annotation { "Feature Type Name" : "Feature", "Feature Type Description" : "" }
export const myFeature = defineFeature(function(context is Context, id is Id, definition is map)
    precondition{}
    {
        {
            var Q0;
            Q0=qCreatedBy(makeId("Front.planeOp"),FACE);
            var sketch = newSketch(context, id + "F0", { "sketchPlane" : qUnion([Q0])});
            skFitSpline(sketch, "E0", {"points": [v(-3.73, -24.98) * mm, v(-7.65, -24.83) * mm, v(-12.44, -18.15) * mm, v(-12.87, -5.52) * mm, v(-17.38, -7.12) * mm, v(-18.97, -20.91) * mm, v(-14.76, -31.66) * mm, v(-14.04, -37.46) * mm, v(-21.44, -52.13) * mm, v(-22.46, -57.8) * mm, v(-21.59, -62.3) * mm, v(-19.4, -65.05) * mm, v(-17.23, -67.38) * mm, v(-11.57, -70.43) * mm, v(-1.26, -72.9) * mm, v(9.49, -73.19) * mm, v(18.93, -67.96) * mm, v(21.69, -60.84) * mm, v(15.73, -44.43) * mm, v(14.72, -38.92) * mm, v(18.2, -30.5) * mm, v(17.33, -25.7) * mm, v(12.97, -30.93) * mm, v(5.57, -30.5) * mm, v(4.26, -24.54) * mm], "startDerivative": vector(-129.19, -19.7) * mm, "endDerivative": vector(5.95, 184.87) * mm});
            skLineSegment(sketch, "E1", {"start": v(-3.73, -24.98) * mm, "end": v(4.26, -25.17) * mm});
            skLineSegment(sketch, "E2", {"start": v(4.26, -25.17) * mm, "end": v(4.26, -24.54) * mm});
            skSolve(sketch);
        }
        {
            var Q0;
            Q0 = qSketchRegion(id + "F0", true);
            extrude(context, id + "F1", {"entities" : qUnion([Q0]), "depth" : 7.62 * mm});
        }
        {
            var Q0;
            Q0=makeQuery(id+"F1.opExtrude","CAP_FACE",FACE,{"disambiguationData":[OSD([sQuery(id+"F0.wireOp",EDGE,"E0"),sQuery(id+"F0.wireOp",EDGE,"E1")])],"isStart":false});
            var sketch = newSketch(context, id + "F2", { "sketchPlane" : qUnion([Q0])});
            skLineSegment(sketch, "E3.bottom", {"start": v(-10.16, -39.56) * mm, "end": v(10.16, -39.56) * mm});
            skLineSegment(sketch, "E3.top", {"start": v(-10.16, -44.4) * mm, "end": v(10.16, -44.4) * mm});
            skLineSegment(sketch, "E3.left", {"start": v(-10.16, -39.56) * mm, "end": v(-10.16, -44.4) * mm});
            skLineSegment(sketch, "E3.right", {"start": v(10.16, -39.56) * mm, "end": v(10.16, -44.4) * mm});
            skPoint(sketch, "E3.middle", {"position": v(0, -41.99) * mm});
            skSolve(sketch);
        }
        {
            var Q0;
            Q0 = qSketchRegion(id + "F2", true);
            extrude(context, id + "F3", {"entities" : qUnion([Q0]), "operationType" : NewBodyOperationType.ADD, "depth" : 1.02 * mm});
        }
        {
            var Q0;
            Q0=makeQuery(id+"F3.opExtrude","CAP_FACE",FACE,{"disambiguationData":[OSD([sQuery(id+"F2.wireOp",EDGE,"E3.bottom"),sQuery(id+"F2.wireOp",EDGE,"E3.top"),sQuery(id+"F2.wireOp",EDGE,"E3.left"),sQuery(id+"F2.wireOp",EDGE,"E3.right")])],"isStart":false});
            var sketch = newSketch(context, id + "F4", { "sketchPlane" : qUnion([Q0])});
            skText(sketch, "E4", { "text": "Peter Robles\n", "fontName": "OpenSans-Regular.ttf"});
            const initialGuessF4  = {"E4": [-0.01016, -0.04322, 1, 0, 0.00248]};
            skSetInitialGuess(sketch, initialGuessF4);
            skSolve(sketch);
        }
        {
            var Q0;
            Q0 = qSketchRegion(id + "F4", true);
            extrude(context, id + "F5", {"entities" : qUnion([Q0]), "operationType" : NewBodyOperationType.ADD, "depth" : 0.76 * mm});
        }
        {
            var Q0;
            {var subQ0=sQuery(id+"F0.wireOp",EDGE,"E1");var subQ1=sQuery(id+"F0.wireOp",EDGE,"E0");Q0=makeQuery(id+"F1.opExtrude","SWEPT_FACE",FACE,{"disambiguationData":[OSD([subQ0]),TDD([makeQuery(id+"F0.imprint","IMPRINT",EDGE,{"disambiguationData":[TD([[makeQuery(id+"F0.imprint","INTERSECT",VERTEX,{"disambiguationData":[OD(0.0)],"derivedFrom":[subQ1,subQ0]}),-1.0]])],"derivedFrom":subQ0})])]});}
            var sketch = newSketch(context, id + "F6", { "sketchPlane" : qUnion([Q0])});
            skCircle(sketch, "E5", {"center": v(0.87, -3.81) * mm, "radius": 3.16 * mm});
            skSolve(sketch);
        }
        {
            var Q0;
            Q0 = qSketchRegion(id + "F6", true);
            extrude(context, id + "F7", {"entities" : qUnion([Q0]), "operationType" : NewBodyOperationType.REMOVE, "oppositeDirection" : true, "depth" : 12.7 * mm});
        }
        {
            var Q0;
            Q0=qCreatedBy(makeId("Right.planeOp"),FACE);
            var sketch = newSketch(context, id + "F8", { "sketchPlane" : qUnion([Q0])});
            skFitSpline(sketch, "E6", {"points": [v(0, -42.77) * mm, v(13.98, -43.74) * mm, v(17.88, -67.36) * mm], "startDerivative": vector(39.85, 7.14) * mm, "endDerivative": vector(32.57, -55.77) * mm});
            skSolve(sketch);
        }
        {
            var Q0;
            Q0=makeQuery(id+"F1.opExtrude","CAP_FACE",FACE,{"disambiguationData":[OSD([sQuery(id+"F0.wireOp",EDGE,"E0"),sQuery(id+"F0.wireOp",EDGE,"E1")])],"isStart":true});
            var sketch = newSketch(context, id + "F9", { "sketchPlane" : qUnion([Q0])});
            skLineSegment(sketch, "E7.0.0", {"start": v(3.73, -24.98) * mm, "end": v(-4.24, -25.17) * mm});
            skFitSpline(sketch, "E7.0.1", {"points": [v(-4.26, -24.54) * mm, v(-4.19, -26.8) * mm, v(-4.03, -31.58) * mm, v(-13.94, -33.1) * mm, v(-17.47, -22.72) * mm, v(-19.31, -31.55) * mm, v(-13.59, -38.96) * mm, v(-15.52, -44.44) * mm, v(-23.64, -60.95) * mm, v(-19.58, -68.45) * mm, v(-9.5, -74.5) * mm, v(1.17, -73.03) * mm, v(11.38, -70.96) * mm, v(17.34, -67.7) * mm, v(19.3, -65.02) * mm, v(22.06, -62.48) * mm, v(22.59, -57.44) * mm, v(22.37, -51.95) * mm, v(12.49, -37.55) * mm, v(14.6, -31.5) * mm, v(20.22, -21.4) * mm, v(19.65, -6.72) * mm, v(10.27, -3.17) * mm, v(14.6, -18.92) * mm, v(8.11, -25.64) * mm, v(5, -25.17) * mm, v(3.73, -24.98) * mm]});
            skPoint(sketch, "E8.0", {"position": v(0, -42.77) * mm});
            skLineSegment(sketch, "E9.bottom", {"start": v(-3.05, -39.72) * mm, "end": v(3.05, -39.72) * mm});
            skLineSegment(sketch, "E9.top", {"start": v(-3.05, -45.81) * mm, "end": v(3.05, -45.81) * mm});
            skLineSegment(sketch, "E9.left", {"start": v(-3.05, -39.72) * mm, "end": v(-3.05, -45.81) * mm});
            skLineSegment(sketch, "E9.right", {"start": v(3.05, -39.72) * mm, "end": v(3.05, -45.81) * mm});
            skSolve(sketch);
        }
        {
            var Q0;
            Q0=makeQuery(id+"F9.imprint","IMPRINT",FACE,{"disambiguationData":[TD([[makeQuery(id+"F9.imprint","IMPRINT",EDGE,{"derivedFrom":sQuery(id+"F9.wireOp",EDGE,"E9.bottom")}),-1.0]])]});
            var Q1;
            Q1=sQuery(id+"F8.wireOp",EDGE,"E6");
            sweep(context, id + "F10", {"operationType" : NewBodyOperationType.ADD, "profiles" : qUnion([Q0]), "path" : qUnion([Q1])});
        }
        {
            var Q0;
            Q0=makeQuery(id+"F1.opExtrude","CAP_FACE",FACE,{"disambiguationData":[OSD([sQuery(id+"F0.wireOp",EDGE,"E0"),sQuery(id+"F0.wireOp",EDGE,"E1")])],"isStart":false});
            var sketch = newSketch(context, id + "F11", { "sketchPlane" : qUnion([Q0])});
            skCircle(sketch, "E10", {"center": v(14.16, -57.35) * mm, "radius": 2.37 * mm});
            skSolve(sketch);
        }
        {
            var Q0;
            Q0 = qSketchRegion(id + "F11", true);
            extrude(context, id + "F12", {"entities" : qUnion([Q0]), "operationType" : NewBodyOperationType.ADD, "depth" : 1.27 * mm});
        }
        {
            var Q0;
            Q0=makeQuery(id+"F12.opExtrude","CAP_FACE",FACE,{"disambiguationData":[OSD([sQuery(id+"F11.wireOp",EDGE,"E10")])],"isStart":false});
            var sketch = newSketch(context, id + "F13", { "sketchPlane" : qUnion([Q0])});
            skCircle(sketch, "E11", {"center": v(14.16, -57.35) * mm, "radius": 1.33 * mm});
            skSolve(sketch);
        }
        {
            var Q0;
            Q0 = qSketchRegion(id + "F13", true);
            extrude(context, id + "F14", {"entities" : qUnion([Q0]), "operationType" : NewBodyOperationType.ADD, "depth" : 0.5 * mm});
        }
        {
            var Q0;
            Q0=makeQuery(id+"F10.opSweep","CAP_FACE",FACE,{"disambiguationData":[OSD([sQuery(id+"F8.wireOp",VERTEX,"E6.end"),sQuery(id+"F9.wireOp",EDGE,"E9.bottom"),sQuery(id+"F9.wireOp",EDGE,"E9.top"),sQuery(id+"F9.wireOp",EDGE,"E9.left"),sQuery(id+"F9.wireOp",EDGE,"E9.right")])],"isStart":false});
            var sketch = newSketch(context, id + "F15", { "sketchPlane" : qUnion([Q0])});
            skLineSegment(sketch, "E12.bottom", {"start": v(9.6, 3.35) * mm, "end": v(-9.6, 3.35) * mm});
            skLineSegment(sketch, "E12.top", {"start": v(9.6, 9.44) * mm, "end": v(-9.6, 9.44) * mm});
            skLineSegment(sketch, "E12.left", {"start": v(9.6, 3.35) * mm, "end": v(9.6, 9.44) * mm});
            skLineSegment(sketch, "E12.right", {"start": v(-9.6, 3.35) * mm, "end": v(-9.6, 9.44) * mm});
            skPoint(sketch, "E12.middle", {"position": v(0, 6.4) * mm});
            skPoint(sketch, "E12.middle.positionSnap0", {"position": v(3.05, 6.4) * mm});
            skPoint(sketch, "E12.middle.positionSnap1", {"position": v(0, 3.35) * mm});
            skPoint(sketch, "E12.centerSnap0", {"position": v(3.05, 6.4) * mm});
            skPoint(sketch, "E12.centerSnap1", {"position": v(0, 3.35) * mm});
            skSolve(sketch);
        }
        {
            var Q0;
            Q0 = qSketchRegion(id + "F15", true);
            extrude(context, id + "F16", {"entities" : qUnion([Q0]), "operationType" : NewBodyOperationType.ADD, "depth" : 2.03 * mm, "offsetDistance" : 25.4 * mm});
        }
        {
            var Q0;
            Q0=makeQuery(id+"F1.opExtrude","SWEPT_BODY",BODY,{"disambiguationData":[OSD([sQuery(id+"F0.wireOp",EDGE,"E0"),sQuery(id+"F0.wireOp",EDGE,"E1"),sQuery(id+"F0.wireOp",EDGE,"E2")])]});
            deleteBodies(context, id + "F17", {"entities" : qUnion([Q0])});
        }
    });